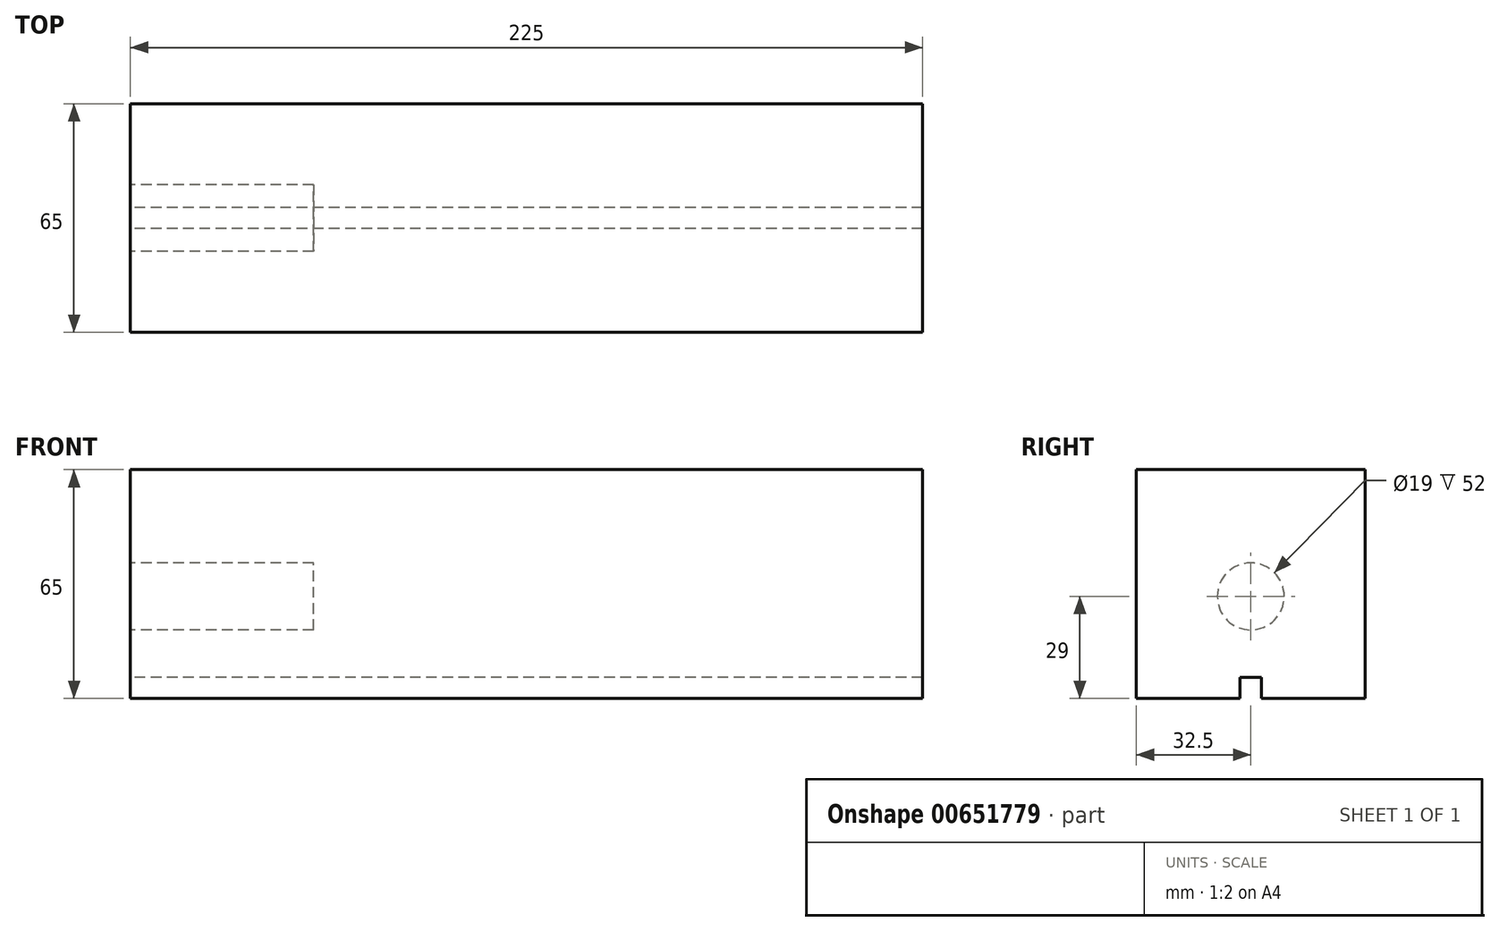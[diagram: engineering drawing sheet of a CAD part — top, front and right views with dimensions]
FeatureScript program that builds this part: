
annotation { "Feature Type Name" : "Feature", "Feature Type Description" : "" }
export const myFeature = defineFeature(function(context is Context, id is Id, definition is map)
    precondition{}
    {
        {
            var Q0;
            Q0=qCreatedBy(makeId("Right.planeOp"),FACE);
            var sketch = newSketch(context, id + "F0", { "sketchPlane" : qUnion([Q0])});
            skLineSegment(sketch, "E0.bottom", {"start": v(0, 0) * mm, "end": v(32.5, 0) * mm});
            skLineSegment(sketch, "E0.top", {"start": v(0, 65) * mm, "end": v(32.5, 65) * mm});
            skLineSegment(sketch, "E0.left", {"start": v(0, 6) * mm, "end": v(0, 65) * mm});
            skLineSegment(sketch, "E0.right", {"start": v(32.5, 0) * mm, "end": v(32.5, 65) * mm});
            skLineSegment(sketch, "E1", {"start": v(3, 0) * mm, "end": v(3, 6) * mm});
            skLineSegment(sketch, "E2", {"start": v(3, 6) * mm, "end": v(0, 6) * mm});
            skPoint(sketch, "E3", {"position": v(0, 29) * mm});
            skSolve(sketch);
        }
        {
            var Q0;
            Q0=makeQuery(id+"F0.imprint","IMPRINT",FACE,{"disambiguationData":[TD([[makeQuery(id+"F0.imprint","IMPRINT",EDGE,{"derivedFrom":sQuery(id+"F0.wireOp",EDGE,"E0.top")}),-1.0]])]});
            extrude(context, id + "F1", {"entities" : qUnion([Q0]), "depth" : 225 * mm, "offsetDistance" : 25 * mm});
        }
        {
            var Q0;
            Q0=makeQuery(id+"F1.opExtrude","SWEPT_BODY",BODY,{"disambiguationData":[OSD([sQuery(id+"F0.wireOp",EDGE,"E0.bottom"),sQuery(id+"F0.wireOp",EDGE,"E0.top"),sQuery(id+"F0.wireOp",EDGE,"E0.left"),sQuery(id+"F0.wireOp",EDGE,"E0.right"),sQuery(id+"F0.wireOp",EDGE,"E1"),sQuery(id+"F0.wireOp",EDGE,"E2")])]});
            var Q1;
            Q1=qCreatedBy(makeId("Front.planeOp"),FACE);
            mirror(context, id + "F2", {"operationType" : NewBodyOperationType.ADD, "entities" : qUnion([Q0]), "mirrorPlane" : qUnion([Q1])});
        }
        {
            var Q0;
            Q0=qCreatedBy(makeId("Right.planeOp"),FACE);
            var sketch = newSketch(context, id + "F3", { "sketchPlane" : qUnion([Q0])});
            skCircle(sketch, "E4", {"center": v(0, 29) * mm, "radius": 9.5 * mm});
            skSolve(sketch);
        }
        {
            var Q0;
            Q0=makeQuery(id+"F3.imprint","IMPRINT",FACE,{"disambiguationData":[TD([[makeQuery(id+"F3.imprint","IMPRINT",EDGE,{"derivedFrom":sQuery(id+"F3.wireOp",EDGE,"E4")}),1.0]])]});
            extrude(context, id + "F4", {"entities" : qUnion([Q0]), "operationType" : NewBodyOperationType.REMOVE, "depth" : 52 * mm, "offsetDistance" : 25 * mm});
        }
    });
